# Revit family: Haworth_Epure_ProximityStorage_JuxtaposedModule_EU_PRELIMINARY
name_source: partatom
category: Furniture
units: mm (PartAtom-declared; Revit-internal decimal feet)

## family parameters
Always vertical = Yes
Cut with Voids When Loaded = No
OmniClass Number = 23.40.70.14.64.11
OmniClass Title = Office Furniture
Room Calculation Point = No
Shared = No
Work Plane-Based = No

## types (4) — shared parameters
Actual Depth = 45 cm
Actual Height = 69 cm
Actual Width = 80 cm
Assembly Code = E2020200
Description = Haworth - Epure - Proximity Storage - Juxtaposed Module
Epure 2 Fixing Kit = No
Fixing 2 Kit = Loadbearing for CPU only
Glide Finish = Haworth _ Polymer _ Black
Handle 1 = No
Handle 2 = No
Manufacturer = Haworth
Model = EUPSDEPXXX
New Tibas 2 Fixing Kit = No
Pencil Tray Finish = Haworth _ Metal _ Structured White EC
Pencil Tray Options = Not for Loadbearing for CPU, Module Freestanding with 1 Suspended Files Drawer
Revision Number = 1
Size = Verify Final Dim.w/ Haworth
Trim Finish = Haworth _ Paint _ Smooth Plaster
URL = https://www.haworth.com
URL - Product = https://www.haworth.com
Warranty = http://www.haworth.com

## per-type parameters (varying)
| type | Below Drawer | Below Pull | Epure 1 Fixing Kit | Metal Handle | New T_Up 1 Fixing Kit | New T_Up 2 Fixing Kit | New Tibas 1 Fixing Kit | Pencil Tray | Upper Pull | with Pull | without Pull |
| Loadbearing for CPU | No | No | No | No | Yes | Yes | No | No | No | No | Yes |
| Freestanding with 1 Shelf | No | No | No | No | No | No | Yes | Yes | No | No | Yes |
| Freestanding with 1 Suspended Files Drawer | Yes | Yes | No | Yes | No | No | No | Yes | No | Yes | No |
| Module Freestanding with 1 Suspended Files Drawer | Yes | Yes | Yes | Yes | No | No | No | No | Yes | Yes | No |

type visibility flags: 4 boolean params named "<type name>" — each type sets only its own to Yes (folded from table)

## geometry (parser evidence)
native form markers: Sweep x15
no freeform markers — native parametric forms only
